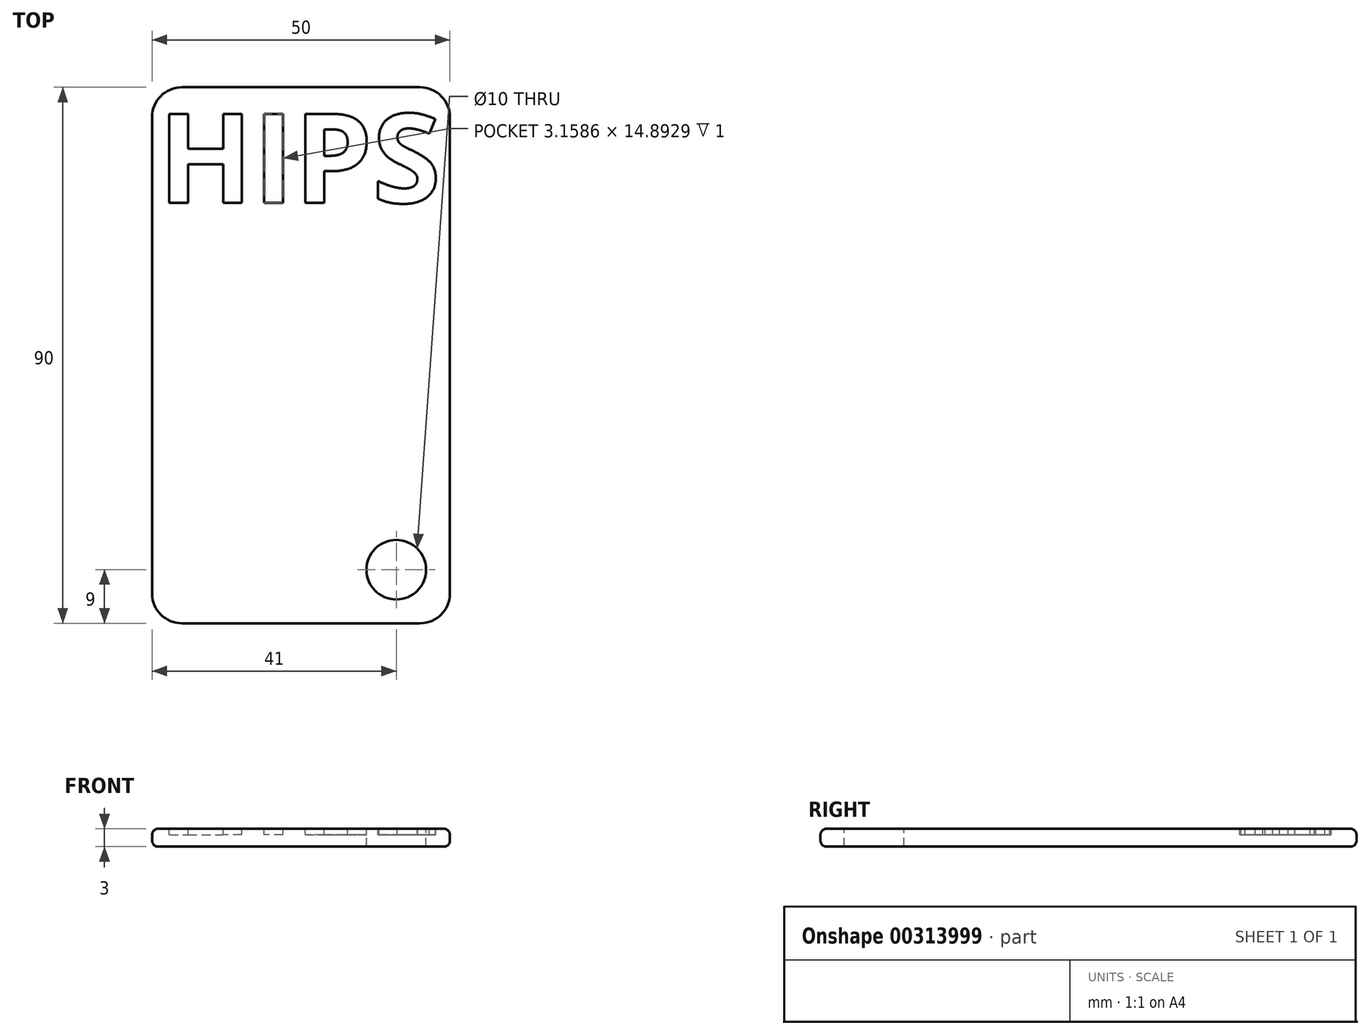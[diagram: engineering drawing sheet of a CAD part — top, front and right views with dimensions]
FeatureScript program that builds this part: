
annotation { "Feature Type Name" : "Feature", "Feature Type Description" : "" }
export const myFeature = defineFeature(function(context is Context, id is Id, definition is map)
    precondition{}
    {
        {
            var Q0;
            Q0=qCreatedBy(makeId("Top.planeOp"),FACE);
            var sketch = newSketch(context, id + "F0", { "sketchPlane" : qUnion([Q0])});
            skLineSegment(sketch, "E0.bottom", {"start": v(-45, 25) * mm, "end": v(45, 25) * mm});
            skLineSegment(sketch, "E0.top", {"start": v(-45, -25) * mm, "end": v(45, -25) * mm});
            skLineSegment(sketch, "E0.left", {"start": v(-45, 25) * mm, "end": v(-45, -25) * mm});
            skLineSegment(sketch, "E0.right", {"start": v(45, 25) * mm, "end": v(45, -25) * mm});
            skLineSegment(sketch, "E1", {"start": v(-45, 25) * mm, "end": v(45, -25) * mm, "construction": true});
            skSolve(sketch);
        }
        {
            var Q0;
            Q0=makeQuery(id+"F0.imprint","IMPRINT",FACE,{"disambiguationData":[TD([[makeQuery(id+"F0.imprint","IMPRINT",EDGE,{"derivedFrom":sQuery(id+"F0.wireOp",EDGE,"E0.bottom")}),-1.0]])]});
            extrude(context, id + "F1", {"entities" : qUnion([Q0]), "depth" : 3 * mm});
        }
        {
            var Q0;
            Q0=makeQuery(id+"F1.opExtrude","CAP_FACE",FACE,{"disambiguationData":[OSD([sQuery(id+"F0.wireOp",EDGE,"E0.bottom"),sQuery(id+"F0.wireOp",EDGE,"E0.top"),sQuery(id+"F0.wireOp",EDGE,"E0.left"),sQuery(id+"F0.wireOp",EDGE,"E0.right")])],"isStart":false});
            var Q1;
            Q1=makeQuery(id+"F1.opExtrude","CAP_FACE",FACE,{"disambiguationData":[OSD([sQuery(id+"F0.wireOp",EDGE,"E0.bottom"),sQuery(id+"F0.wireOp",EDGE,"E0.top"),sQuery(id+"F0.wireOp",EDGE,"E0.left"),sQuery(id+"F0.wireOp",EDGE,"E0.right")])],"isStart":true});
            fillet(context, id + "F2", {"entities" : qUnion([Q0, Q1]), "radius" : 1 * mm, "tangentPropagation" : true, "allowEdgeOverflow" : false});
        }
        {
            var Q0;
            Q0=makeQuery(id+"F1.opExtrude","SWEPT_EDGE",EDGE,{"disambiguationData":[OSD([sQuery(id+"F0.wireOp",EDGE,"E0.top"),sQuery(id+"F0.wireOp",EDGE,"E0.right")])]});
            var Q1;
            Q1=makeQuery(id+"F1.opExtrude","SWEPT_EDGE",EDGE,{"disambiguationData":[OSD([sQuery(id+"F0.wireOp",EDGE,"E0.bottom"),sQuery(id+"F0.wireOp",EDGE,"E0.right")])]});
            var Q2;
            Q2=makeQuery(id+"F1.opExtrude","SWEPT_EDGE",EDGE,{"disambiguationData":[OSD([sQuery(id+"F0.wireOp",EDGE,"E0.bottom"),sQuery(id+"F0.wireOp",EDGE,"E0.left")])]});
            var Q3;
            Q3=makeQuery(id+"F1.opExtrude","SWEPT_EDGE",EDGE,{"disambiguationData":[OSD([sQuery(id+"F0.wireOp",EDGE,"E0.top"),sQuery(id+"F0.wireOp",EDGE,"E0.left")])]});
            fillet(context, id + "F3", {"entities" : qUnion([Q0, Q1, Q2, Q3]), "radius" : 5 * mm, "tangentPropagation" : true, "allowEdgeOverflow" : false});
        }
        {
            var Q0;
            Q0=qCreatedBy(makeId("Right.planeOp"),FACE);
            var sketch = newSketch(context, id + "F4", { "sketchPlane" : qUnion([Q0])});
            skLineSegment(sketch, "E2", {"start": v(0, 0) * mm, "end": v(0, 32.9) * mm});
            skSolve(sketch);
        }
        {
            var Q0;
            Q0=makeQuery(id+"F1.opExtrude","SWEPT_BODY",BODY,{"disambiguationData":[OSD([sQuery(id+"F0.wireOp",EDGE,"E0.bottom"),sQuery(id+"F0.wireOp",EDGE,"E0.top"),sQuery(id+"F0.wireOp",EDGE,"E0.left"),sQuery(id+"F0.wireOp",EDGE,"E0.right")])]});
            var Q1;
            Q1=sQuery(id+"F4.wireOp",EDGE,"E2");
            transform(context, id + "F5", {"entities" : qUnion([Q0]), "transformType" : TransformType.ROTATION, "transformAxis" : qUnion([Q1]), "angle" : 90 * degree, "makeCopy" : false});
        }
        {
            var Q0;
            Q0=makeQuery(id+"F1.opExtrude","CAP_FACE",FACE,{"disambiguationData":[OSD([sQuery(id+"F0.wireOp",EDGE,"E0.bottom"),sQuery(id+"F0.wireOp",EDGE,"E0.top"),sQuery(id+"F0.wireOp",EDGE,"E0.left"),sQuery(id+"F0.wireOp",EDGE,"E0.right")])],"isStart":false});
            var sketch = newSketch(context, id + "F6", { "sketchPlane" : qUnion([Q0])});
            skText(sketch, "E3", { "text": "HIPS", "fontName": "OpenSans-Bold.ttf"});
            const initialGuessF6  = {"E3": [-0.024, 0.02562, 1, 0, 0.01502]};
            skSetInitialGuess(sketch, initialGuessF6);
            skSolve(sketch);
        }
        {
            var Q0;
            Q0=qSketchRegion(id+"F6",true);
            extrude(context, id + "F7", {"entities" : qUnion([Q0]), "operationType" : NewBodyOperationType.REMOVE, "oppositeDirection" : true, "depth" : 1 * mm});
        }
        {
            var Q0;
            {var subQ0=sQuery(id+"F0.wireOp",EDGE,"E0.left");var subQ2=sQuery(id+"F0.wireOp",EDGE,"E0.bottom");var subQ4=sQuery(id+"F0.wireOp",EDGE,"E0.right");var subQ6=sQuery(id+"F0.wireOp",EDGE,"E0.top");Q0=makeQuery(id+"F7.boolean.opBoolean","SPLIT",FACE,{"disambiguationData":[TD([makeQuery(id+"F7.opExtrude","SWEPT_FACE",FACE,{"disambiguationData":[OSD([sQuery(id+"F6.wireOp",EDGE,"E3.sketch_text.stroke-0")])]})])],"derivedFrom":makeQuery(id+"F1.opExtrude","CAP_FACE",FACE,{"disambiguationData":[OSD([subQ2,subQ6,subQ0,subQ4])],"isStart":false})});}
            var sketch = newSketch(context, id + "F8", { "sketchPlane" : qUnion([Q0])});
            skCircle(sketch, "E4", {"center": v(16, -36) * mm, "radius": 5 * mm});
            skSolve(sketch);
        }
        {
            var Q0;
            Q0=qSketchRegion(id+"F8",true);
            extrude(context, id + "F9", {"entities" : qUnion([Q0]), "operationType" : NewBodyOperationType.REMOVE, "oppositeDirection" : true, "depth" : 3 * mm});
        }
    });
